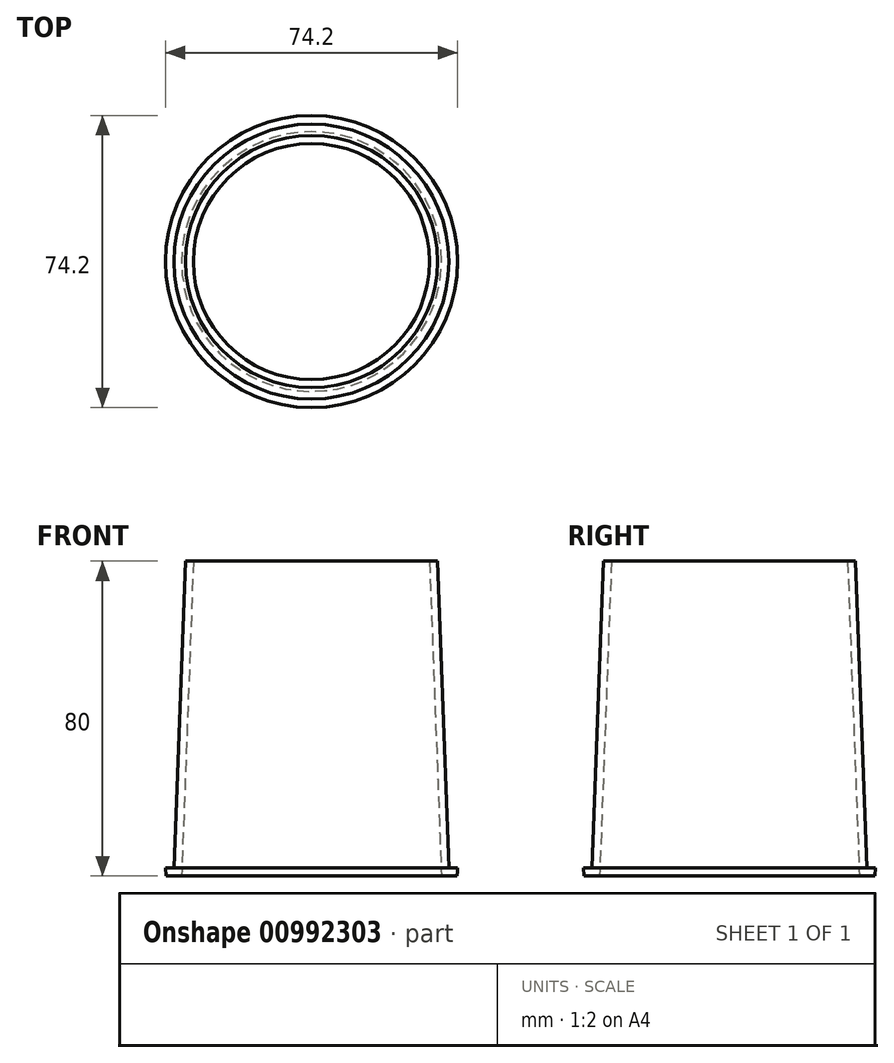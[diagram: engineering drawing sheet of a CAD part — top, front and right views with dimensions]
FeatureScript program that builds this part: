
annotation { "Feature Type Name" : "Feature", "Feature Type Description" : "" }
export const myFeature = defineFeature(function(context is Context, id is Id, definition is map)
    precondition{}
    {
        {
            var Q0;
            Q0=qCreatedBy(makeId("Top.planeOp"),FACE);
            var sketch = newSketch(context, id + "F0", { "sketchPlane" : qUnion([Q0])});
            skCircle(sketch, "E0", {"center": v(0, 0) * mm, "radius": 37 * mm});
            skCircle(sketch, "E1", {"center": v(0, 0) * mm, "radius": 35 * mm});
            skSolve(sketch);
        }
        {
            var Q0;
            Q0=qCreatedBy(makeId("Top.planeOp"),FACE);
            cPlane(context, id + "F1", {"entities" : qUnion([Q0]), "cplaneType" : CPlaneType.OFFSET, "offset" : 80 * mm, "width" : 150 * mm, "height" : 150 * mm});
        }
        {
            var Q0;
            Q0=qCreatedBy(id+"F1.planeOp",FACE);
            var sketch = newSketch(context, id + "F2", { "sketchPlane" : qUnion([Q0])});
            skCircle(sketch, "E2", {"center": v(0, 0) * mm, "radius": 32 * mm});
            skSolve(sketch);
        }
        {
            var Q0;
            Q0=makeQuery(id+"F0.imprint","IMPRINT",FACE,{"disambiguationData":[TD([[makeQuery(id+"F0.imprint","IMPRINT",EDGE,{"derivedFrom":sQuery(id+"F0.wireOp",EDGE,"E1")}),1.0]])]});
            var Q1;
            Q1=makeQuery(id+"F2.imprint","IMPRINT",FACE,{"disambiguationData":[TD([[makeQuery(id+"F2.imprint","IMPRINT",EDGE,{"derivedFrom":sQuery(id+"F2.wireOp",EDGE,"E2")}),1.0]])]});
            var Q2;
            Q2=makeQuery(id+"F0.imprint","IMPRINT",FACE,{"disambiguationData":[TD([[makeQuery(id+"F0.imprint","IMPRINT",EDGE,{"derivedFrom":sQuery(id+"F0.wireOp",EDGE,"E1")}),1.0]])]});
            var Q3;
            Q3=makeQuery(id+"F2.imprint","IMPRINT",FACE,{"disambiguationData":[TD([[makeQuery(id+"F2.imprint","IMPRINT",EDGE,{"derivedFrom":sQuery(id+"F2.wireOp",EDGE,"E2")}),1.0]])]});
            loft(context, id + "F3", {"sheetProfilesArray" : [{ "sheetProfileEntities" : qUnion([Q0]) }, { "sheetProfileEntities" : qUnion([Q1]) }], "wireProfilesArray" : [{ "wireProfileEntities" : qUnion([Q2]) }, { "wireProfileEntities" : qUnion([Q3]) }]});
        }
        {
            var Q0;
            Q0=makeQuery(id+"F0.imprint","IMPRINT",FACE,{"disambiguationData":[TD([[makeQuery(id+"F0.imprint","IMPRINT",EDGE,{"derivedFrom":sQuery(id+"F0.wireOp",EDGE,"E0")}),1.0]])]});
            extrude(context, id + "F4", {"entities" : qUnion([Q0]), "operationType" : NewBodyOperationType.ADD, "depth" : 2 * mm, "offsetDistance" : 25 * mm, "hasDraft" : true, "draftAngle" : 3 * degree});
        }
        {
            var Q0;
            {var subQ0=sQuery(id+"F0.wireOp",EDGE,"E1");Q0=makeQuery(id+"F4.boolean.opBoolean","MERGE",FACE,{"derivedFrom":[makeQuery(id+"F3.opLoft","CAP_FACE",FACE,{"disambiguationData":[OSD([makeQuery(id+"F0.imprint","IMPRINT",FACE,{"disambiguationData":[TD([[makeQuery(id+"F0.imprint","IMPRINT",EDGE,{"derivedFrom":subQ0}),1.0]])]})])],"isStart":true}),makeQuery(id+"F4.opExtrude","CAP_FACE",FACE,{"disambiguationData":[OSD([sQuery(id+"F0.wireOp",EDGE,"E0"),subQ0])],"isStart":true})]});}
            var Q1;
            Q1=makeQuery(id+"F3.opLoft","CAP_FACE",FACE,{"disambiguationData":[OSD([makeQuery(id+"F2.imprint","IMPRINT",FACE,{"disambiguationData":[TD([[makeQuery(id+"F2.imprint","IMPRINT",EDGE,{"derivedFrom":sQuery(id+"F2.wireOp",EDGE,"E2")}),1.0]])]})])],"isStart":true});
            shell(context, id + "F5", {"entities" : qUnion([Q0, Q1]), "thickness" : 2 * mm});
        }
    });
